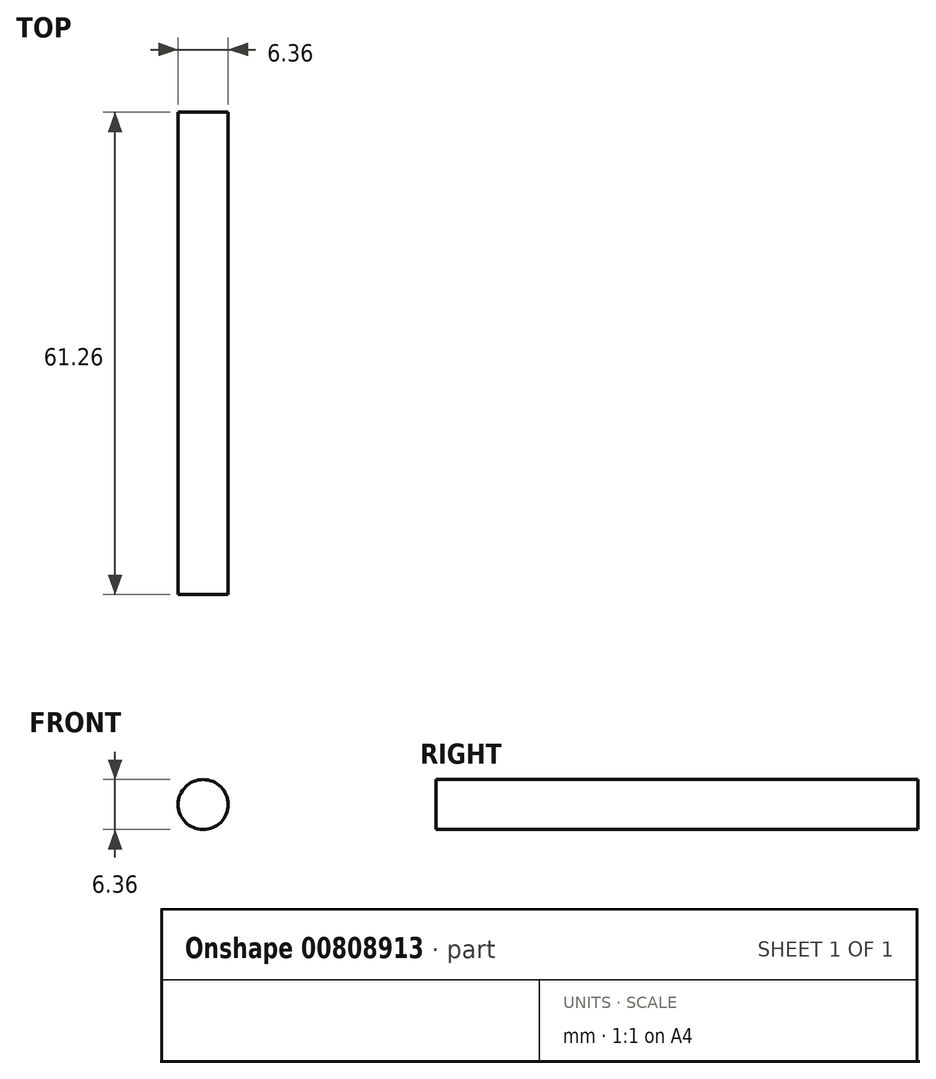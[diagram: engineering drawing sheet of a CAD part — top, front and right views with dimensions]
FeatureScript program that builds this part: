
annotation { "Feature Type Name" : "Feature", "Feature Type Description" : "" }
export const myFeature = defineFeature(function(context is Context, id is Id, definition is map)
    precondition{}
    {
        {
            var Q0;
            Q0=qCreatedBy(makeId("Front.planeOp"),FACE);
            var sketch = newSketch(context, id + "F0", { "sketchPlane" : qUnion([Q0])});
            skCircle(sketch, "E0", {"center": v(0, 0) * mm, "radius": 3.18 * mm});
            skSolve(sketch);
        }
        {
            var Q0;
            Q0 = qSketchRegion(id + "F0", true);
            extrude(context, id + "F1", {"entities" : qUnion([Q0]), "depth" : 61.26 * mm, "offsetDistance" : 25.4 * mm});
        }
    });
